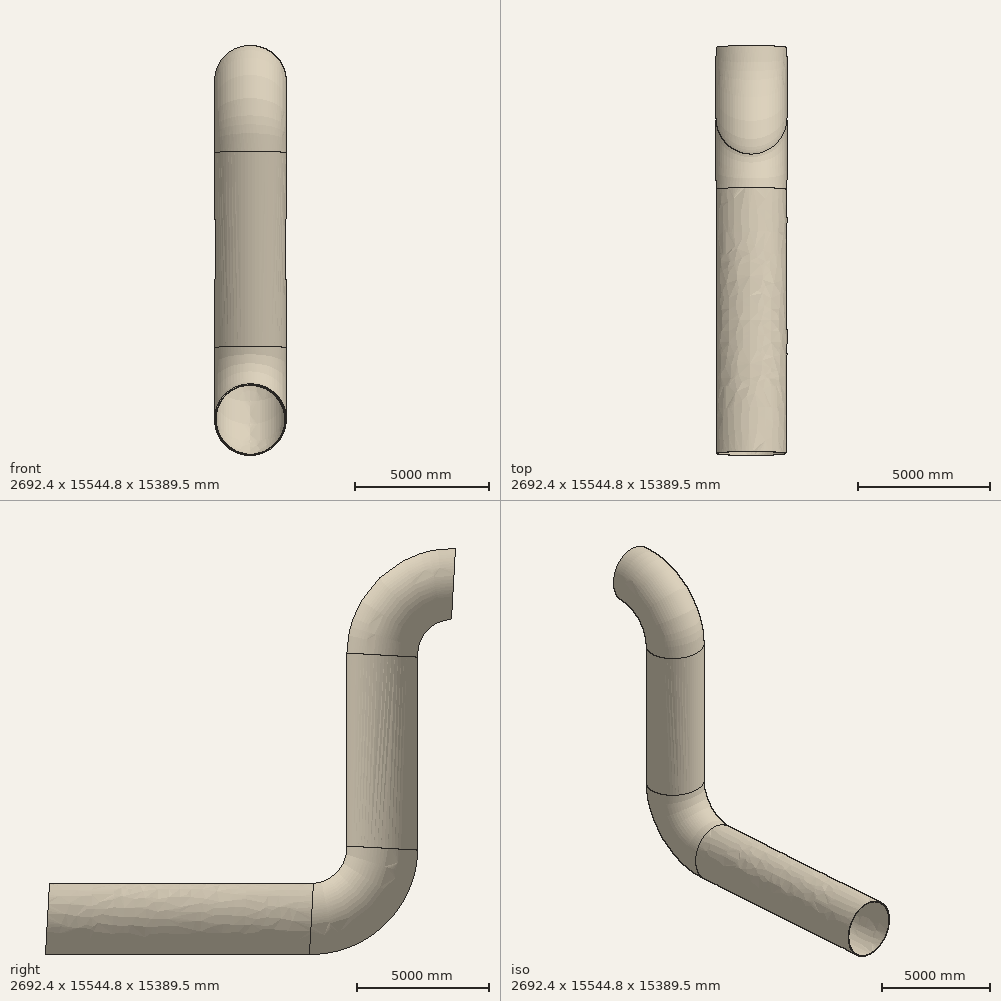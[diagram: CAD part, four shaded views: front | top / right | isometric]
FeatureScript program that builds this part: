
annotation { "Feature Type Name" : "Feature", "Feature Type Description" : "" }
export const myFeature = defineFeature(function(context is Context, id is Id, definition is map)
    precondition{}
    {
        {
            var Q0;
            Q0=qCreatedBy(makeId("Front.planeOp"),FACE);
            var sketch = newSketch(context, id + "F0", { "sketchPlane" : qUnion([Q0])});
            skCircle(sketch, "E0", {"center": v(0, 0) * mm, "radius": 1346.2 * mm});
            skCircle(sketch, "E1", {"center": v(0, 0) * mm, "radius": 1308.1 * mm});
            skSolve(sketch);
        }
        {
            var Q0;
            Q0=qCreatedBy(makeId("Right.planeOp"),FACE);
            var sketch = newSketch(context, id + "F1", { "sketchPlane" : qUnion([Q0])});
            skLineSegment(sketch, "E2", {"start": v(152.4, 0) * mm, "end": v(0, 0) * mm});
            skLineSegment(sketch, "E3", {"start": v(-2540, -2692.4) * mm, "end": v(-2540, -10007.6) * mm});
            skLineSegment(sketch, "E4", {"start": v(-5232.4, -12700) * mm, "end": v(-15240, -12700) * mm});
            skPoint(sketch, "E5.visualSharp", {"position": v(-2540, 0) * mm});
            skArc(sketch, "E5.filletArc", {"start": v(152.4, 0) * mm, "mid": v(-1751.41, -788.59) * mm, "end": v(-2540, -2692.4) * mm});
            skPoint(sketch, "E6.visualSharp", {"position": v(-2540, -12700) * mm});
            skArc(sketch, "E6.filletArc", {"start": v(-5232.4, -12700) * mm, "mid": v(-3328.59, -11911.41) * mm, "end": v(-2540, -10007.6) * mm});
            skSolve(sketch);
        }
        {
            var Q0;
            Q0=makeQuery(id+"F0.imprint","IMPRINT",FACE,{"disambiguationData":[TD([[makeQuery(id+"F0.imprint","IMPRINT",EDGE,{"derivedFrom":sQuery(id+"F0.wireOp",EDGE,"E0")}),1.0]])]});
            var Q1;
            Q1=sQuery(id+"F1.wireOp",EDGE,"E5.filletArc");
            var Q2;
            Q2=sQuery(id+"F1.wireOp",EDGE,"E3");
            var Q3;
            Q3=sQuery(id+"F1.wireOp",EDGE,"E6.filletArc");
            var Q4;
            Q4=sQuery(id+"F1.wireOp",EDGE,"E4");
            sweep(context, id + "F2", {"profiles" : qUnion([Q0]), "path" : qUnion([Q1, Q2, Q3, Q4])});
        }
    });
